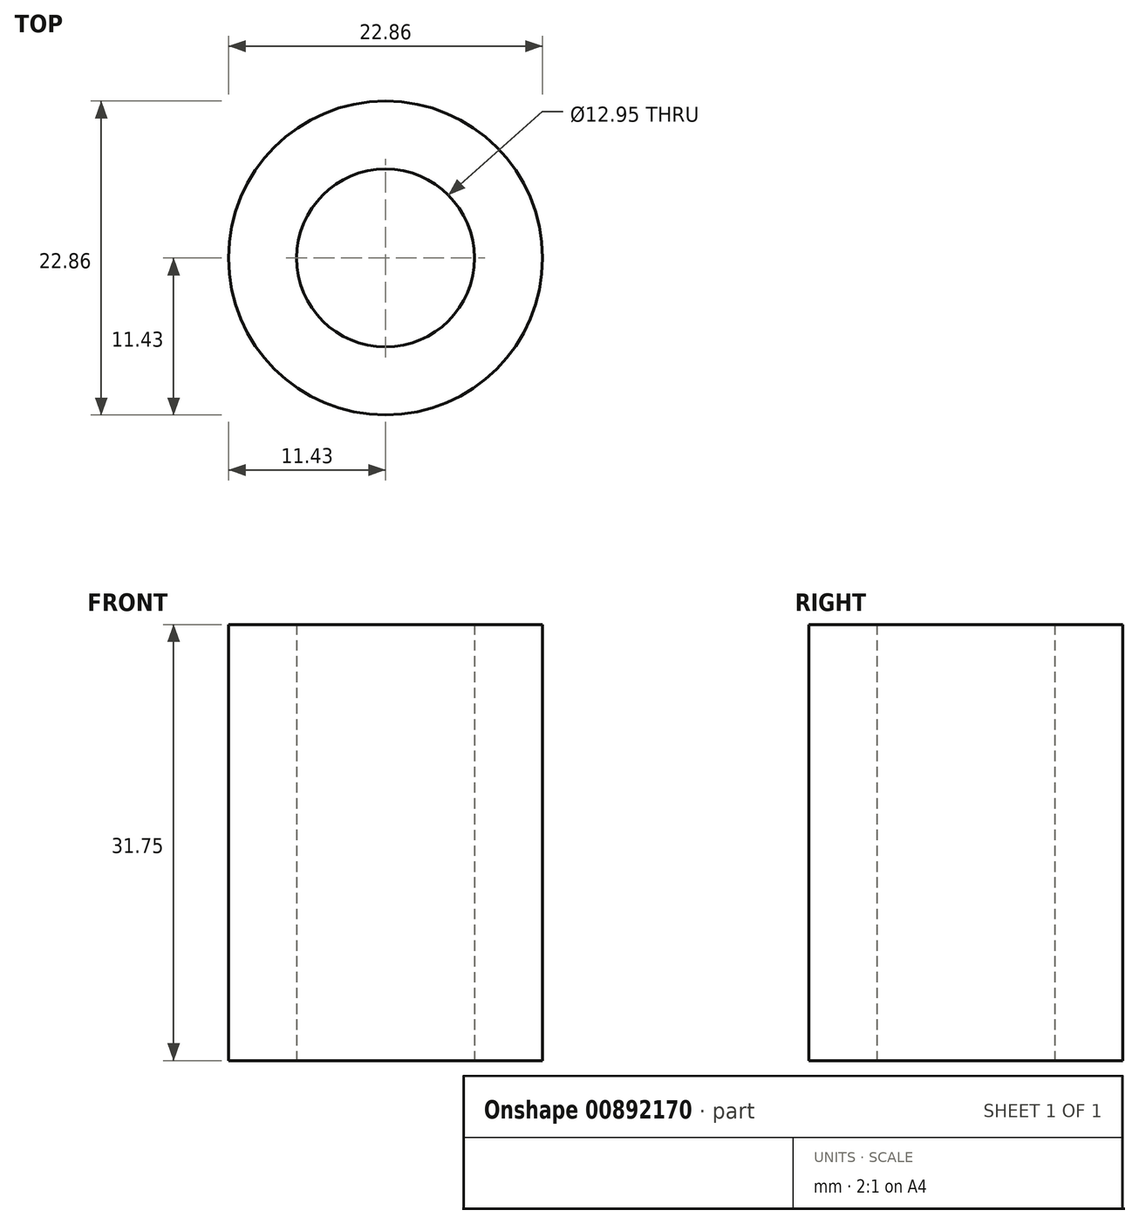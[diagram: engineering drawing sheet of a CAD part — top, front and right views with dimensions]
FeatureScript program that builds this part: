
annotation { "Feature Type Name" : "Feature", "Feature Type Description" : "" }
export const myFeature = defineFeature(function(context is Context, id is Id, definition is map)
    precondition{}
    {
        {
            var Q0;
            Q0=qCreatedBy(makeId("Top.planeOp"),FACE);
            var sketch = newSketch(context, id + "F0", { "sketchPlane" : qUnion([Q0])});
            skCircle(sketch, "E0", {"center": v(0, 0) * mm, "radius": 6.48 * mm});
            skCircle(sketch, "E1", {"center": v(0, 0) * mm, "radius": 11.43 * mm});
            skSolve(sketch);
        }
        {
            var Q0;
            Q0 = qSketchRegion(id + "F0", true);
            extrude(context, id + "F1", {"entities" : qUnion([Q0]), "depth" : 31.75 * mm, "offsetDistance" : 25.4 * mm});
        }
    });
